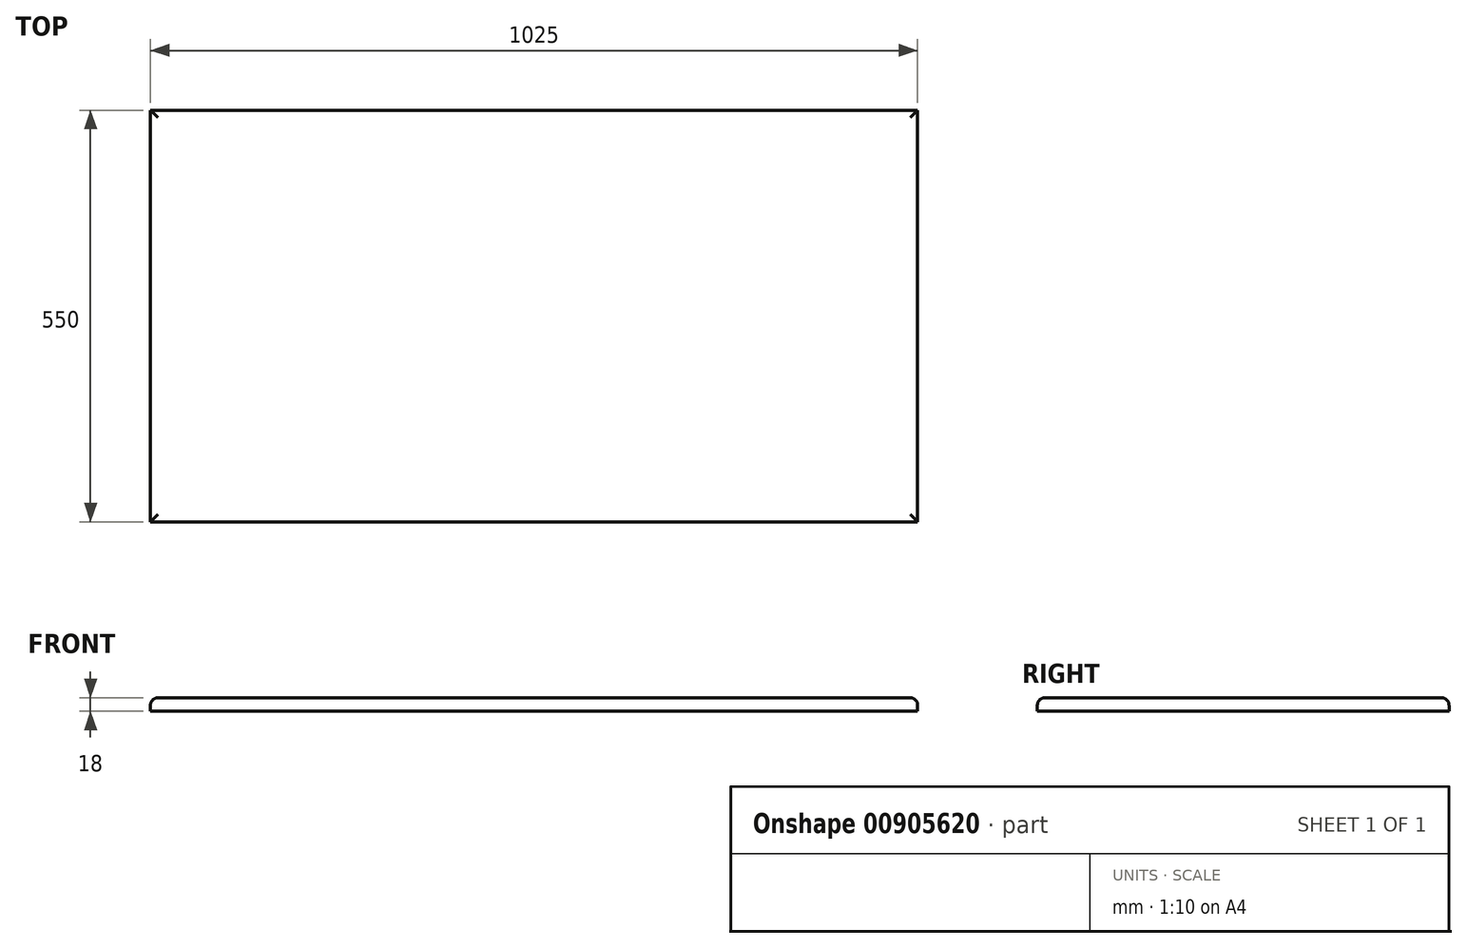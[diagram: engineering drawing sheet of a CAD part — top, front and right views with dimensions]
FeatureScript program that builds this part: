
annotation { "Feature Type Name" : "Feature", "Feature Type Description" : "" }
export const myFeature = defineFeature(function(context is Context, id is Id, definition is map)
    precondition{}
    {
        {
            var Q0;
            Q0=qCreatedBy(makeId("Top.planeOp"),FACE);
            var sketch = newSketch(context, id + "F0", { "sketchPlane" : qUnion([Q0])});
            skLineSegment(sketch, "E0.bottom", {"start": v(512.5, 275) * mm, "end": v(-512.5, 275) * mm});
            skLineSegment(sketch, "E0.top", {"start": v(512.5, -275) * mm, "end": v(-512.5, -275) * mm});
            skLineSegment(sketch, "E0.left", {"start": v(512.5, 275) * mm, "end": v(512.5, -275) * mm});
            skLineSegment(sketch, "E0.right", {"start": v(-512.5, 275) * mm, "end": v(-512.5, -275) * mm});
            skPoint(sketch, "E0.middle", {"position": v(0, 0) * mm});
            skSolve(sketch);
        }
        {
            var Q0;
            Q0=qSketchRegion(id+"F0",true);
            extrude(context, id + "F1", {"entities" : qUnion([Q0]), "depth" : 18 * mm, "offsetDistance" : 25 * mm});
        }
        {
            var Q0;
            Q0=makeQuery(id+"F1.opExtrude","CAP_EDGE",EDGE,{"disambiguationData":[OSD([sQuery(id+"F0.wireOp",EDGE,"E0.top")])],"isStart":false});
            var Q1;
            Q1=makeQuery(id+"F1.opExtrude","CAP_EDGE",EDGE,{"disambiguationData":[OSD([sQuery(id+"F0.wireOp",EDGE,"E0.right")])],"isStart":false});
            var Q2;
            Q2=makeQuery(id+"F1.opExtrude","CAP_EDGE",EDGE,{"disambiguationData":[OSD([sQuery(id+"F0.wireOp",EDGE,"E0.bottom")])],"isStart":false});
            var Q3;
            Q3=makeQuery(id+"F1.opExtrude","CAP_EDGE",EDGE,{"disambiguationData":[OSD([sQuery(id+"F0.wireOp",EDGE,"E0.left")])],"isStart":false});
            fillet(context, id + "F2", {"entities" : qUnion([Q0, Q1, Q2, Q3]), "radius" : 10 * mm, "tangentPropagation" : true, "allowEdgeOverflow" : false});
        }
    });
